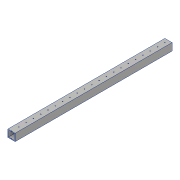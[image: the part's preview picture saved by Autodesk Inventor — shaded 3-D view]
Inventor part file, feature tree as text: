
AUTODESK INVENTOR PART (.ipt)
format: ipt  version: 2018 (Build 220112000, 112)  size: 136,704 bytes
history: native  units: in
note: dims shown in document units (in); Inventor stores cm internally (conversion verified against a paired STEP export)
features: sketch x2, extrude x1, shell x1, hole x1
ambient origin geometry x8: Origin, YZ Plane, XZ Plane, XY Plane, X Axis, Y Axis, Z Axis, Center Point
bodies: Solid1 (feature_tree)
feature tree (5):
  extrude  "Extrusion1"  Depth=1.0in
  shell  "Shell1"  Thickness=21.5in
  hole  "Hole1"  [1 undecoded]
  sketch  "Sketch1"  dims[d0=1.0in d1=1.0in d2=21.5in d3=0.0in]
  sketch  "Sketch2"  dims[d4=0.1in d5=0.5in d6=0.5in d7=14.5669in d9=1.0in d10=0.3937in d12=1.0in d14=0.1in d15=0.75in d16=0.375in d17=0.25in d18=0.5635in d19=2.0in d20=0.8108in]
note: 1 required parameter value undecoded (feature->parameter linkage not recoverable at this tier; creation-order binding heuristic only, values carry confidence <= 0.55)
